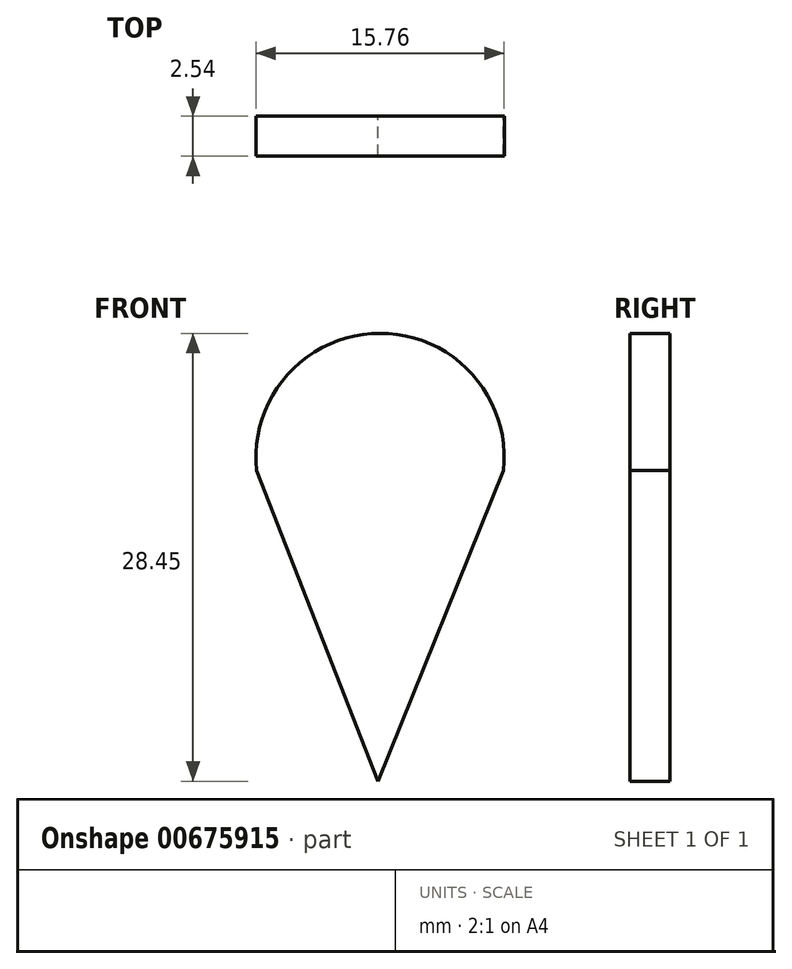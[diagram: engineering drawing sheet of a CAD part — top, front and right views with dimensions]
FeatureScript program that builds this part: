
annotation { "Feature Type Name" : "Feature", "Feature Type Description" : "" }
export const myFeature = defineFeature(function(context is Context, id is Id, definition is map)
    precondition{}
    {
        {
            var Q0;
            Q0=qCreatedBy(makeId("Front.planeOp"),FACE);
            var sketch = newSketch(context, id + "F0", { "sketchPlane" : qUnion([Q0])});
            skLineSegment(sketch, "E0", {"start": v(0, -12.67) * mm, "end": v(-7.7, 7.07) * mm});
            skLineSegment(sketch, "E1", {"start": v(0, -12.67) * mm, "end": v(7.97, 7.07) * mm});
            skArc(sketch, "E2", {"start": v(7.97, 7.07) * mm, "mid": v(0.13, 15.78) * mm, "end": v(-7.7, 7.07) * mm});
            skPoint(sketch, "E3.orphan", {"position": v(10, 12.1) * mm});
            skPoint(sketch, "E4.orphan", {"position": v(-9.67, 12.1) * mm});
            skPoint(sketch, "E5.end.orphan", {"position": v(-0.16, 12.1) * mm});
            skLineSegment(sketch, "E6", {"start": v(7.97, 7.07) * mm, "end": v(-7.7, 7.07) * mm});
            skPoint(sketch, "E7", {"position": v(-7.7, 7.07) * mm});
            skSolve(sketch);
        }
        {
            var Q0;
            Q0 = qSketchRegion(id + "F0", true);
            extrude(context, id + "F1", {"entities" : qUnion([Q0]), "depth" : 2.54 * mm, "offsetDistance" : 25.4 * mm});
        }
    });
